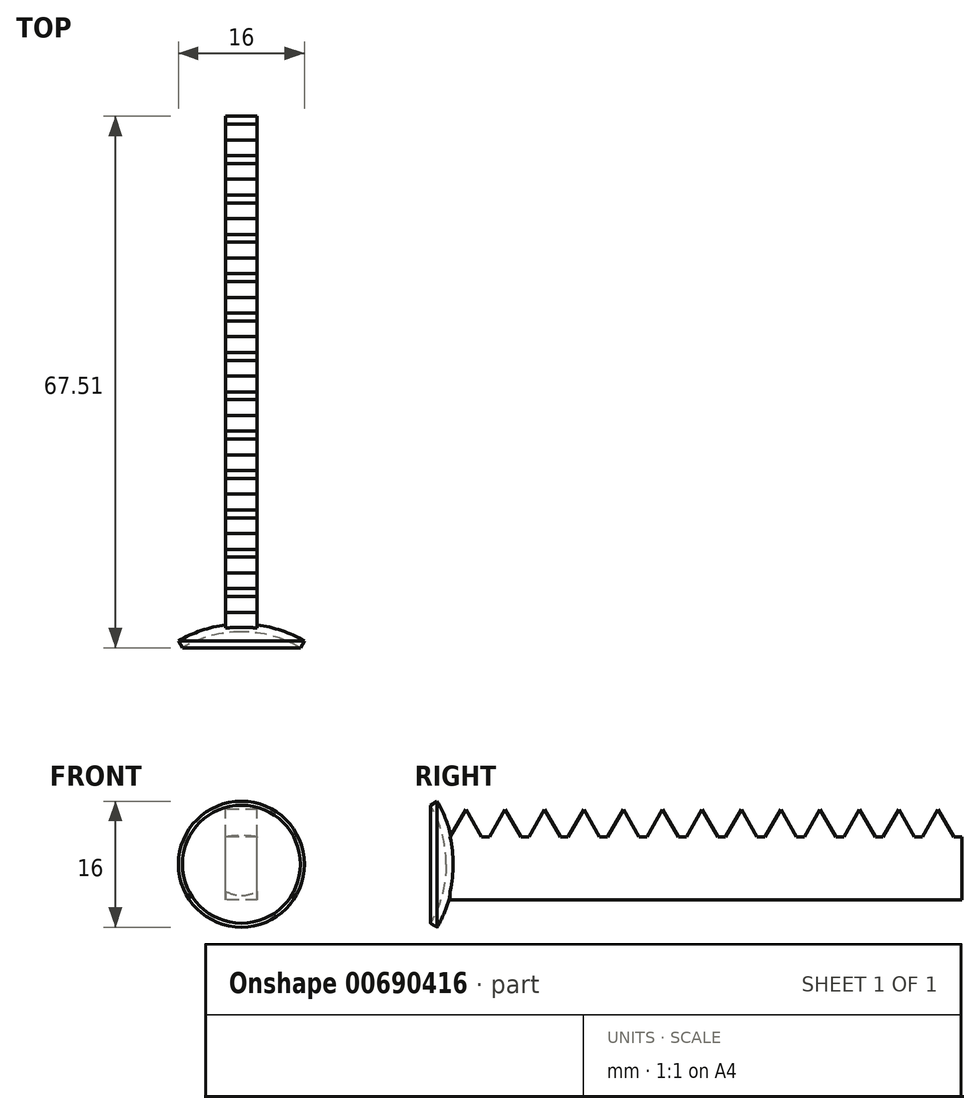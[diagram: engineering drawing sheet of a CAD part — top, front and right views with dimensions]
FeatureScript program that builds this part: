
annotation { "Feature Type Name" : "Feature", "Feature Type Description" : "" }
export const myFeature = defineFeature(function(context is Context, id is Id, definition is map)
    precondition{}
    {
        {
            var Q0;
            Q0=qCreatedBy(makeId("Right.planeOp"),FACE);
            var sketch = newSketch(context, id + "F0", { "sketchPlane" : qUnion([Q0])});
            skLineSegment(sketch, "E0", {"start": v(0, 0) * mm, "end": v(65, 0) * mm});
            skLineSegment(sketch, "E1", {"start": v(65, 0) * mm, "end": v(65, 8) * mm});
            skLineSegment(sketch, "E2", {"start": v(0, 8) * mm, "end": v(0, 0) * mm});
            skLineSegment(sketch, "E3", {"start": v(0, 8) * mm, "end": v(2, 11.46) * mm});
            skLineSegment(sketch, "E4", {"start": v(2, 11.46) * mm, "end": v(4, 8) * mm});
            skLineSegment(sketch, "E5", {"start": v(4, 8) * mm, "end": v(2, 11.46) * mm});
            skLineSegment(sketch, "E6", {"start": v(4, 8) * mm, "end": v(5, 8) * mm});
            skLineSegment(sketch, "E7.1.0.0", {"start": v(5, 8) * mm, "end": v(7, 11.46) * mm});
            skLineSegment(sketch, "E7.1.0.1", {"start": v(9, 8) * mm, "end": v(7, 11.46) * mm});
            skLineSegment(sketch, "E7.1.0.2", {"start": v(7, 11.46) * mm, "end": v(9, 8) * mm});
            skLineSegment(sketch, "E7.1.0.3", {"start": v(9, 8) * mm, "end": v(10, 8) * mm});
            skLineSegment(sketch, "E7.2.0.0", {"start": v(10, 8) * mm, "end": v(12, 11.46) * mm});
            skLineSegment(sketch, "E7.2.0.1", {"start": v(14, 8) * mm, "end": v(12, 11.46) * mm});
            skLineSegment(sketch, "E7.2.0.2", {"start": v(12, 11.46) * mm, "end": v(14, 8) * mm});
            skLineSegment(sketch, "E7.2.0.3", {"start": v(14, 8) * mm, "end": v(15, 8) * mm});
            skLineSegment(sketch, "E7.3.0.0", {"start": v(15, 8) * mm, "end": v(17, 11.46) * mm});
            skLineSegment(sketch, "E7.3.0.1", {"start": v(19, 8) * mm, "end": v(17, 11.46) * mm});
            skLineSegment(sketch, "E7.3.0.2", {"start": v(17, 11.46) * mm, "end": v(19, 8) * mm});
            skLineSegment(sketch, "E7.3.0.3", {"start": v(19, 8) * mm, "end": v(20, 8) * mm});
            skLineSegment(sketch, "E7.4.0.0", {"start": v(20, 8) * mm, "end": v(22, 11.46) * mm});
            skLineSegment(sketch, "E7.4.0.1", {"start": v(24, 8) * mm, "end": v(22, 11.46) * mm});
            skLineSegment(sketch, "E7.4.0.2", {"start": v(22, 11.46) * mm, "end": v(24, 8) * mm});
            skLineSegment(sketch, "E7.4.0.3", {"start": v(24, 8) * mm, "end": v(25, 8) * mm});
            skLineSegment(sketch, "E7.5.0.0", {"start": v(25, 8) * mm, "end": v(27, 11.46) * mm});
            skLineSegment(sketch, "E7.5.0.1", {"start": v(29, 8) * mm, "end": v(27, 11.46) * mm});
            skLineSegment(sketch, "E7.5.0.2", {"start": v(27, 11.46) * mm, "end": v(29, 8) * mm});
            skLineSegment(sketch, "E7.5.0.3", {"start": v(29, 8) * mm, "end": v(30, 8) * mm});
            skLineSegment(sketch, "E7.6.0.0", {"start": v(30, 8) * mm, "end": v(32, 11.46) * mm});
            skLineSegment(sketch, "E7.6.0.1", {"start": v(34, 8) * mm, "end": v(32, 11.46) * mm});
            skLineSegment(sketch, "E7.6.0.2", {"start": v(32, 11.46) * mm, "end": v(34, 8) * mm});
            skLineSegment(sketch, "E7.6.0.3", {"start": v(34, 8) * mm, "end": v(35, 8) * mm});
            skLineSegment(sketch, "E7.7.0.0", {"start": v(35, 8) * mm, "end": v(37, 11.46) * mm});
            skLineSegment(sketch, "E7.7.0.1", {"start": v(39, 8) * mm, "end": v(37, 11.46) * mm});
            skLineSegment(sketch, "E7.7.0.2", {"start": v(37, 11.46) * mm, "end": v(39, 8) * mm});
            skLineSegment(sketch, "E7.7.0.3", {"start": v(39, 8) * mm, "end": v(40, 8) * mm});
            skLineSegment(sketch, "E7.8.0.0", {"start": v(40, 8) * mm, "end": v(42, 11.46) * mm});
            skLineSegment(sketch, "E7.8.0.1", {"start": v(44, 8) * mm, "end": v(42, 11.46) * mm});
            skLineSegment(sketch, "E7.8.0.2", {"start": v(42, 11.46) * mm, "end": v(44, 8) * mm});
            skLineSegment(sketch, "E7.8.0.3", {"start": v(44, 8) * mm, "end": v(45, 8) * mm});
            skLineSegment(sketch, "E7.9.0.0", {"start": v(45, 8) * mm, "end": v(47, 11.46) * mm});
            skLineSegment(sketch, "E7.9.0.1", {"start": v(49, 8) * mm, "end": v(47, 11.46) * mm});
            skLineSegment(sketch, "E7.9.0.2", {"start": v(47, 11.46) * mm, "end": v(49, 8) * mm});
            skLineSegment(sketch, "E7.9.0.3", {"start": v(49, 8) * mm, "end": v(50, 8) * mm});
            skLineSegment(sketch, "E7.10.0.0", {"start": v(50, 8) * mm, "end": v(52, 11.46) * mm});
            skLineSegment(sketch, "E7.10.0.1", {"start": v(54, 8) * mm, "end": v(52, 11.46) * mm});
            skLineSegment(sketch, "E7.10.0.2", {"start": v(52, 11.46) * mm, "end": v(54, 8) * mm});
            skLineSegment(sketch, "E7.10.0.3", {"start": v(54, 8) * mm, "end": v(55, 8) * mm});
            skLineSegment(sketch, "E7.11.0.0", {"start": v(55, 8) * mm, "end": v(57, 11.46) * mm});
            skLineSegment(sketch, "E7.11.0.1", {"start": v(59, 8) * mm, "end": v(57, 11.46) * mm});
            skLineSegment(sketch, "E7.11.0.2", {"start": v(57, 11.46) * mm, "end": v(59, 8) * mm});
            skLineSegment(sketch, "E7.11.0.3", {"start": v(59, 8) * mm, "end": v(60, 8) * mm});
            skLineSegment(sketch, "E7.12.0.0", {"start": v(60, 8) * mm, "end": v(62, 11.46) * mm});
            skLineSegment(sketch, "E7.12.0.1", {"start": v(64, 8) * mm, "end": v(62, 11.46) * mm});
            skLineSegment(sketch, "E7.12.0.2", {"start": v(62, 11.46) * mm, "end": v(64, 8) * mm});
            skLineSegment(sketch, "E7.12.0.3", {"start": v(64, 8) * mm, "end": v(65, 8) * mm});
            skLineSegment(sketch, "E7.direction1", {"start": v(0, 8) * mm, "end": v(5, 8) * mm, "construction": true});
            skSolve(sketch);
        }
        {
            var Q0;
            Q0=qSketchRegion(id+"F0",true);
            extrude(context, id + "F1", {"entities" : qUnion([Q0]), "depth" : 2 * mm, "offsetDistance" : 25 * mm, "hasSecondDirection" : true, "secondDirectionOppositeDirection" : true, "secondDirectionDepth" : 2 * mm});
        }
        {
            var Q0;
            Q0=qCreatedBy(makeId("Right.planeOp"),FACE);
            var sketch = newSketch(context, id + "F2", { "sketchPlane" : qUnion([Q0])});
            skArc(sketch, "E8", {"start": v(-0.5, 4.5) * mm, "mid": v(-1.01, 8.38) * mm, "end": v(-2.5, 12) * mm});
            skLineSegment(sketch, "E9", {"start": v(-2.5, 12) * mm, "end": v(-1.64, 12.5) * mm});
            skArc(sketch, "E10", {"start": v(0.5, 4.5) * mm, "mid": v(-0.05, 8.64) * mm, "end": v(-1.64, 12.5) * mm});
            skLineSegment(sketch, "E11", {"start": v(-0.5, 4.5) * mm, "end": v(0.5, 4.5) * mm});
            skSolve(sketch);
        }
        {
            var Q0;
            Q0=qSketchRegion(id+"F2",true);
            var Q1;
            Q1=sQuery(id+"F2.wireOp",EDGE,"E11");
            revolve(context, id + "F3", {"operationType" : NewBodyOperationType.ADD, "entities" : qUnion([Q0]), "axis" : qUnion([Q1]), "revolveType" : RevolveType.FULL});
        }
    });
